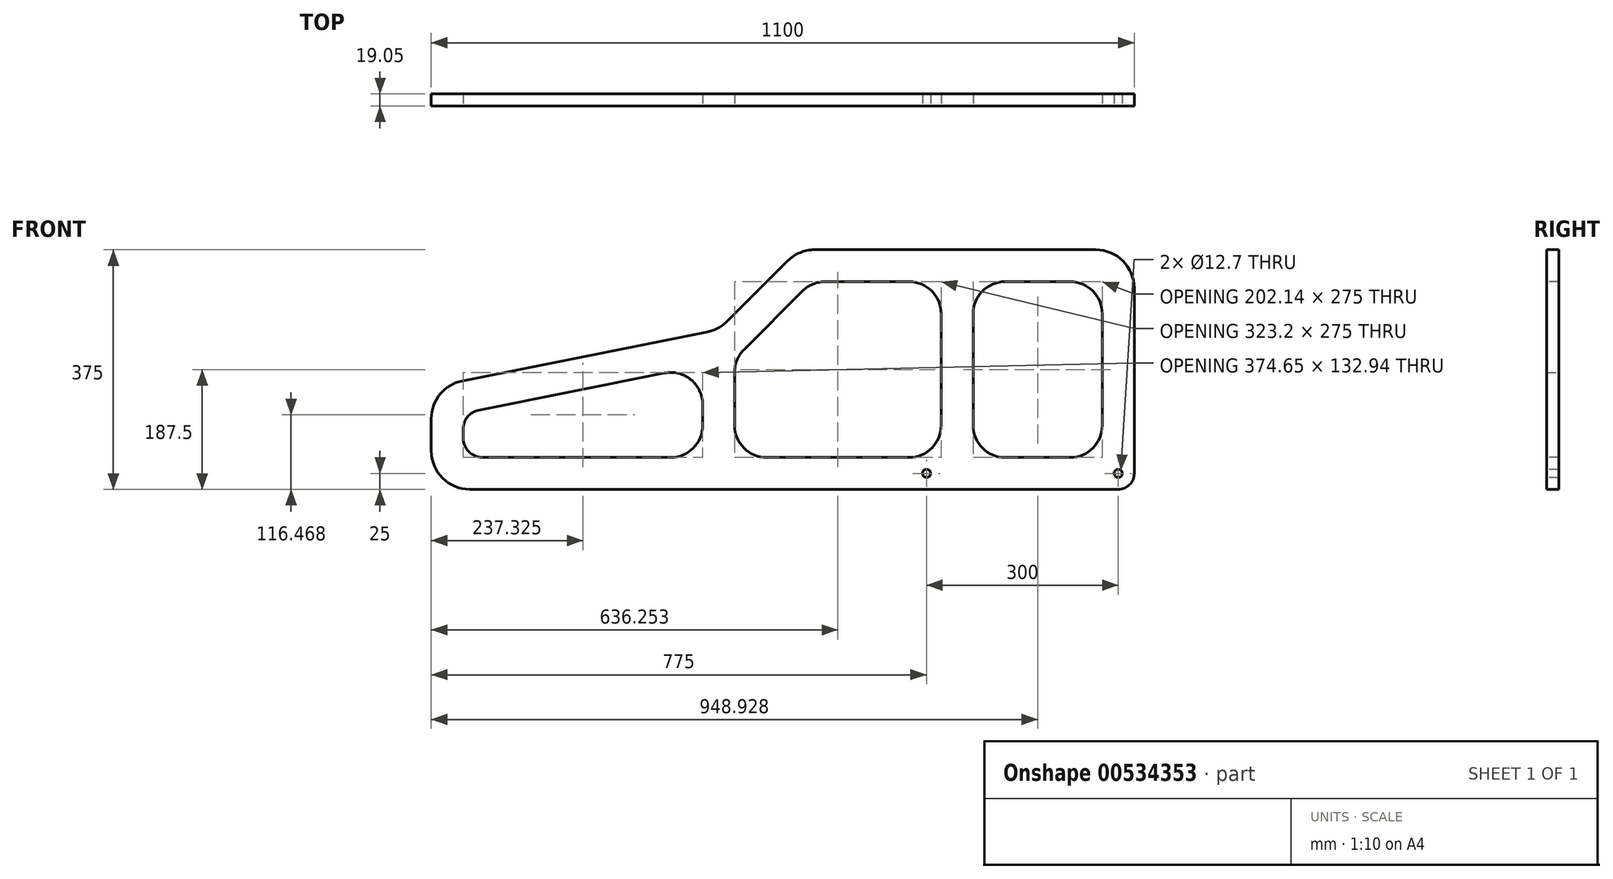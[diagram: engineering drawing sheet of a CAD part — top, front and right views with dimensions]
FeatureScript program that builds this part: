
annotation { "Feature Type Name" : "Feature", "Feature Type Description" : "" }
export const myFeature = defineFeature(function(context is Context, id is Id, definition is map)
    precondition{}
    {
        {
            var Q0;
            Q0=qCreatedBy(makeId("Front.planeOp"),FACE);
            var sketch = newSketch(context, id + "F0", { "sketchPlane" : qUnion([Q0])});
            skLineSegment(sketch, "E0", {"start": v(0, 0) * mm, "end": v(-1100, 0) * mm});
            skLineSegment(sketch, "E1", {"start": v(-1100, 0) * mm, "end": v(-1100, 160) * mm});
            skLineSegment(sketch, "E2", {"start": v(-1100, 160) * mm, "end": v(-650, 250) * mm});
            skLineSegment(sketch, "E3", {"start": v(-650, 250) * mm, "end": v(-525, 375) * mm});
            skLineSegment(sketch, "E4", {"start": v(-525, 375) * mm, "end": v(0, 375) * mm});
            skLineSegment(sketch, "E5", {"start": v(0, 375) * mm, "end": v(0, 0) * mm});
            skSolve(sketch);
        }
        {
            var Q0;
            Q0=makeQuery(id+"F0.imprint","IMPRINT",FACE,{"disambiguationData":[TD([[makeQuery(id+"F0.imprint","IMPRINT",EDGE,{"derivedFrom":sQuery(id+"F0.wireOp",EDGE,"E0")}),-1.0]])]});
            extrude(context, id + "F1", {"entities" : qUnion([Q0]), "depth" : 19.05 * mm, "offsetDistance" : 25 * mm});
        }
        {
            var Q0;
            Q0=makeQuery(id+"F1.opExtrude","CAP_FACE",FACE,{"disambiguationData":[OSD([sQuery(id+"F0.wireOp",EDGE,"E0"),sQuery(id+"F0.wireOp",EDGE,"E1"),sQuery(id+"F0.wireOp",EDGE,"E2"),sQuery(id+"F0.wireOp",EDGE,"E3"),sQuery(id+"F0.wireOp",EDGE,"E4"),sQuery(id+"F0.wireOp",EDGE,"E5")])],"isStart":false});
            var sketch = newSketch(context, id + "F2", { "sketchPlane" : qUnion([Q0])});
            skCircle(sketch, "E6", {"center": v(-325, 25) * mm, "radius": 6.35 * mm});
            skSolve(sketch);
        }
        {
            var Q0;
            Q0=makeQuery(id+"F2.imprint","IMPRINT",FACE,{"disambiguationData":[TD([[makeQuery(id+"F2.imprint","IMPRINT",EDGE,{"derivedFrom":sQuery(id+"F2.wireOp",EDGE,"E6")}),1.0]])]});
            extrude(context, id + "F3", {"entities" : qUnion([Q0]), "operationType" : NewBodyOperationType.REMOVE, "oppositeDirection" : true, "depth" : 25 * mm, "offsetDistance" : 25 * mm});
        }
        {
            var Q0;
            Q0=makeQuery(id+"F1.opExtrude","CAP_FACE",FACE,{"disambiguationData":[OSD([sQuery(id+"F0.wireOp",EDGE,"E0"),sQuery(id+"F0.wireOp",EDGE,"E1"),sQuery(id+"F0.wireOp",EDGE,"E2"),sQuery(id+"F0.wireOp",EDGE,"E3"),sQuery(id+"F0.wireOp",EDGE,"E4"),sQuery(id+"F0.wireOp",EDGE,"E5")])],"isStart":false});
            var sketch = newSketch(context, id + "F4", { "sketchPlane" : qUnion([Q0])});
            skCircle(sketch, "E7", {"center": v(-25, 25) * mm, "radius": 6.35 * mm});
            skSolve(sketch);
        }
        {
            var Q0;
            Q0=makeQuery(id+"F4.imprint","IMPRINT",FACE,{"disambiguationData":[TD([[makeQuery(id+"F4.imprint","IMPRINT",EDGE,{"derivedFrom":sQuery(id+"F4.wireOp",EDGE,"E7")}),1.0]])]});
            extrude(context, id + "F5", {"entities" : qUnion([Q0]), "operationType" : NewBodyOperationType.REMOVE, "oppositeDirection" : true, "depth" : 25 * mm, "offsetDistance" : 25 * mm});
        }
        {
            var Q0;
            Q0 = qSketchRegion(id + "F4", true);
            var Q1;
            Q1=makeQuery(id+"F4.imprint","IMPRINT",FACE,{"disambiguationData":[TD([[makeQuery(id+"F4.imprint","IMPRINT",EDGE,{"derivedFrom":sQuery(id+"F4.wireOp",EDGE,"E7")}),1.0]])]});
            extrude(context, id + "F6", {"entities" : qUnion([Q0, Q1]), "operationType" : NewBodyOperationType.REMOVE, "depth" : 25 * mm, "offsetDistance" : 25 * mm});
        }
        {
            var Q0;
            Q0=makeQuery(id+"F1.opExtrude","CAP_FACE",FACE,{"disambiguationData":[OSD([sQuery(id+"F0.wireOp",EDGE,"E0"),sQuery(id+"F0.wireOp",EDGE,"E1"),sQuery(id+"F0.wireOp",EDGE,"E2"),sQuery(id+"F0.wireOp",EDGE,"E3"),sQuery(id+"F0.wireOp",EDGE,"E4"),sQuery(id+"F0.wireOp",EDGE,"E5")])],"isStart":false});
            var sketch = newSketch(context, id + "F7", { "sketchPlane" : qUnion([Q0])});
            skLineSegment(sketch, "E8.0", {"start": v(-625.35, 203.94) * mm, "end": v(-504.29, 325) * mm});
            skLineSegment(sketch, "E8.1", {"start": v(-50, 325) * mm, "end": v(-50, 50) * mm});
            skLineSegment(sketch, "E8.2", {"start": v(-50, 50) * mm, "end": v(-1050, 50) * mm});
            skLineSegment(sketch, "E8.3", {"start": v(-504.29, 325) * mm, "end": v(-50, 325) * mm});
            skLineSegment(sketch, "E8.4", {"start": v(-1050, 50) * mm, "end": v(-1050, 119) * mm});
            skLineSegment(sketch, "E8.5", {"start": v(-1050, 119) * mm, "end": v(-625.35, 203.94) * mm});
            skLineSegment(sketch, "E9", {"start": v(-625.35, 203.94) * mm, "end": v(-625.35, 50) * mm});
            skLineSegment(sketch, "E10", {"start": v(-675.35, 193.94) * mm, "end": v(-675.35, 50) * mm});
            skLineSegment(sketch, "E11", {"start": v(-302.14, 325) * mm, "end": v(-302.14, 50) * mm});
            skLineSegment(sketch, "E12", {"start": v(-252.14, 325) * mm, "end": v(-252.14, 50) * mm});
            skLineSegment(sketch, "E13", {"start": v(-302.14, 187.5) * mm, "end": v(-252.14, 187.5) * mm, "construction": true});
            skLineSegment(sketch, "E14", {"start": v(-277.14, 325) * mm, "end": v(-277.14, 187.5) * mm, "construction": true});
            skSolve(sketch);
        }
        {
            var Q0;
            {var subQ0=sQuery(id+"F7.wireOp",EDGE,"E8.4");Q0=makeQuery(id+"F7.imprint","IMPRINT",FACE,{"disambiguationData":[TD([[makeQuery(id+"F7.imprint","IMPRINT",EDGE,{"derivedFrom":subQ0}),-1.0]])]});}
            var Q1;
            {var subQ2=sQuery(id+"F7.wireOp",EDGE,"E8.0");Q1=makeQuery(id+"F7.imprint","IMPRINT",FACE,{"disambiguationData":[TD([[makeQuery(id+"F7.imprint","IMPRINT",EDGE,{"derivedFrom":subQ2}),-1.0]])]});}
            var Q2;
            {var subQ0=sQuery(id+"F7.wireOp",EDGE,"E8.1");Q2=makeQuery(id+"F7.imprint","IMPRINT",FACE,{"disambiguationData":[TD([[makeQuery(id+"F7.imprint","IMPRINT",EDGE,{"derivedFrom":subQ0}),-1.0]])]});}
            extrude(context, id + "F8", {"entities" : qUnion([Q0, Q1, Q2]), "operationType" : NewBodyOperationType.REMOVE, "oppositeDirection" : true, "depth" : 25 * mm, "offsetDistance" : 25 * mm});
        }
        {
            var Q0;
            Q0=makeQuery(id+"F8.boolean.opBoolean","COPY",EDGE,{"derivedFrom":makeQuery(id+"F8.opExtrude","SWEPT_EDGE",EDGE,{"disambiguationData":[OSD([sQuery(id+"F7.wireOp",EDGE,"E8.2"),sQuery(id+"F7.wireOp",EDGE,"E10")])]})});
            var Q1;
            Q1=makeQuery(id+"F8.boolean.opBoolean","COPY",EDGE,{"derivedFrom":makeQuery(id+"F8.opExtrude","SWEPT_EDGE",EDGE,{"disambiguationData":[OSD([sQuery(id+"F7.wireOp",EDGE,"E8.5"),sQuery(id+"F7.wireOp",EDGE,"E10")])]})});
            var Q2;
            Q2=makeQuery(id+"F8.boolean.opBoolean","COPY",EDGE,{"derivedFrom":makeQuery(id+"F8.opExtrude","SWEPT_EDGE",EDGE,{"disambiguationData":[OSD([sQuery(id+"F7.wireOp",EDGE,"E8.0"),sQuery(id+"F7.wireOp",EDGE,"E8.5"),sQuery(id+"F7.wireOp",EDGE,"E9")])]})});
            var Q3;
            Q3=makeQuery(id+"F8.boolean.opBoolean","COPY",EDGE,{"derivedFrom":makeQuery(id+"F8.opExtrude","SWEPT_EDGE",EDGE,{"disambiguationData":[OSD([sQuery(id+"F7.wireOp",EDGE,"E8.2"),sQuery(id+"F7.wireOp",EDGE,"E9")])]})});
            var Q4;
            Q4=makeQuery(id+"F8.boolean.opBoolean","COPY",EDGE,{"derivedFrom":makeQuery(id+"F8.opExtrude","SWEPT_EDGE",EDGE,{"disambiguationData":[OSD([sQuery(id+"F7.wireOp",EDGE,"E8.0"),sQuery(id+"F7.wireOp",EDGE,"E8.3")])]})});
            var Q5;
            Q5=makeQuery(id+"F8.boolean.opBoolean","COPY",EDGE,{"derivedFrom":makeQuery(id+"F8.opExtrude","SWEPT_EDGE",EDGE,{"disambiguationData":[OSD([sQuery(id+"F7.wireOp",EDGE,"E8.3"),sQuery(id+"F7.wireOp",EDGE,"E11")])]})});
            var Q6;
            Q6=makeQuery(id+"F8.boolean.opBoolean","COPY",EDGE,{"derivedFrom":makeQuery(id+"F8.opExtrude","SWEPT_EDGE",EDGE,{"disambiguationData":[OSD([sQuery(id+"F7.wireOp",EDGE,"E8.2"),sQuery(id+"F7.wireOp",EDGE,"E11")])]})});
            var Q7;
            Q7=makeQuery(id+"F8.boolean.opBoolean","COPY",EDGE,{"derivedFrom":makeQuery(id+"F8.opExtrude","SWEPT_EDGE",EDGE,{"disambiguationData":[OSD([sQuery(id+"F7.wireOp",EDGE,"E8.1"),sQuery(id+"F7.wireOp",EDGE,"E8.2")])]})});
            var Q8;
            Q8=makeQuery(id+"F8.boolean.opBoolean","COPY",EDGE,{"derivedFrom":makeQuery(id+"F8.opExtrude","SWEPT_EDGE",EDGE,{"disambiguationData":[OSD([sQuery(id+"F7.wireOp",EDGE,"E8.2"),sQuery(id+"F7.wireOp",EDGE,"E12")])]})});
            var Q9;
            Q9=makeQuery(id+"F8.boolean.opBoolean","COPY",EDGE,{"derivedFrom":makeQuery(id+"F8.opExtrude","SWEPT_EDGE",EDGE,{"disambiguationData":[OSD([sQuery(id+"F7.wireOp",EDGE,"E8.3"),sQuery(id+"F7.wireOp",EDGE,"E12")])]})});
            var Q10;
            Q10=makeQuery(id+"F8.boolean.opBoolean","COPY",EDGE,{"derivedFrom":makeQuery(id+"F8.opExtrude","SWEPT_EDGE",EDGE,{"disambiguationData":[OSD([sQuery(id+"F7.wireOp",EDGE,"E8.1"),sQuery(id+"F7.wireOp",EDGE,"E8.3")])]})});
            fillet(context, id + "F9", {"entities" : qUnion([Q0, Q1, Q2, Q3, Q4, Q5, Q6, Q7, Q8, Q9, Q10]), "radius" : 50 * mm, "tangentPropagation" : true, "allowEdgeOverflow" : false});
        }
        {
            var Q0;
            Q0=makeQuery(id+"F1.opExtrude","SWEPT_EDGE",EDGE,{"disambiguationData":[OSD([sQuery(id+"F0.wireOp",EDGE,"E2"),sQuery(id+"F0.wireOp",EDGE,"E3")])]});
            var Q1;
            Q1=makeQuery(id+"F1.opExtrude","SWEPT_EDGE",EDGE,{"disambiguationData":[OSD([sQuery(id+"F0.wireOp",EDGE,"E3"),sQuery(id+"F0.wireOp",EDGE,"E4")])]});
            var Q2;
            Q2=makeQuery(id+"F1.opExtrude","SWEPT_EDGE",EDGE,{"disambiguationData":[OSD([sQuery(id+"F0.wireOp",EDGE,"E4"),sQuery(id+"F0.wireOp",EDGE,"E5")])]});
            var Q3;
            Q3=makeQuery(id+"F1.opExtrude","SWEPT_EDGE",EDGE,{"disambiguationData":[OSD([sQuery(id+"F0.wireOp",EDGE,"E1"),sQuery(id+"F0.wireOp",EDGE,"E2")])]});
            var Q4;
            Q4=makeQuery(id+"F1.opExtrude","SWEPT_EDGE",EDGE,{"disambiguationData":[OSD([sQuery(id+"F0.wireOp",EDGE,"E0"),sQuery(id+"F0.wireOp",EDGE,"E1")])]});
            fillet(context, id + "F10", {"entities" : qUnion([Q0, Q1, Q2, Q3, Q4]), "radius" : 60 * mm, "tangentPropagation" : true, "allowEdgeOverflow" : false});
        }
        {
            var Q0;
            Q0=makeQuery(id+"F1.opExtrude","SWEPT_EDGE",EDGE,{"disambiguationData":[OSD([sQuery(id+"F0.wireOp",EDGE,"E0"),sQuery(id+"F0.wireOp",EDGE,"E5")])]});
            fillet(context, id + "F11", {"entities" : qUnion([Q0]), "radius" : 25 * mm, "tangentPropagation" : true, "allowEdgeOverflow" : false});
        }
        {
            var Q0;
            Q0=makeQuery(id+"F8.boolean.opBoolean","COPY",EDGE,{"derivedFrom":makeQuery(id+"F8.opExtrude","SWEPT_EDGE",EDGE,{"disambiguationData":[OSD([sQuery(id+"F7.wireOp",EDGE,"E8.4"),sQuery(id+"F7.wireOp",EDGE,"E8.5")])]})});
            var Q1;
            Q1=makeQuery(id+"F8.boolean.opBoolean","COPY",EDGE,{"derivedFrom":makeQuery(id+"F8.opExtrude","SWEPT_EDGE",EDGE,{"disambiguationData":[OSD([sQuery(id+"F7.wireOp",EDGE,"E8.2"),sQuery(id+"F7.wireOp",EDGE,"E8.4")])]})});
            fillet(context, id + "F12", {"entities" : qUnion([Q0, Q1]), "radius" : 30 * mm, "tangentPropagation" : true, "allowEdgeOverflow" : false});
        }
    });
